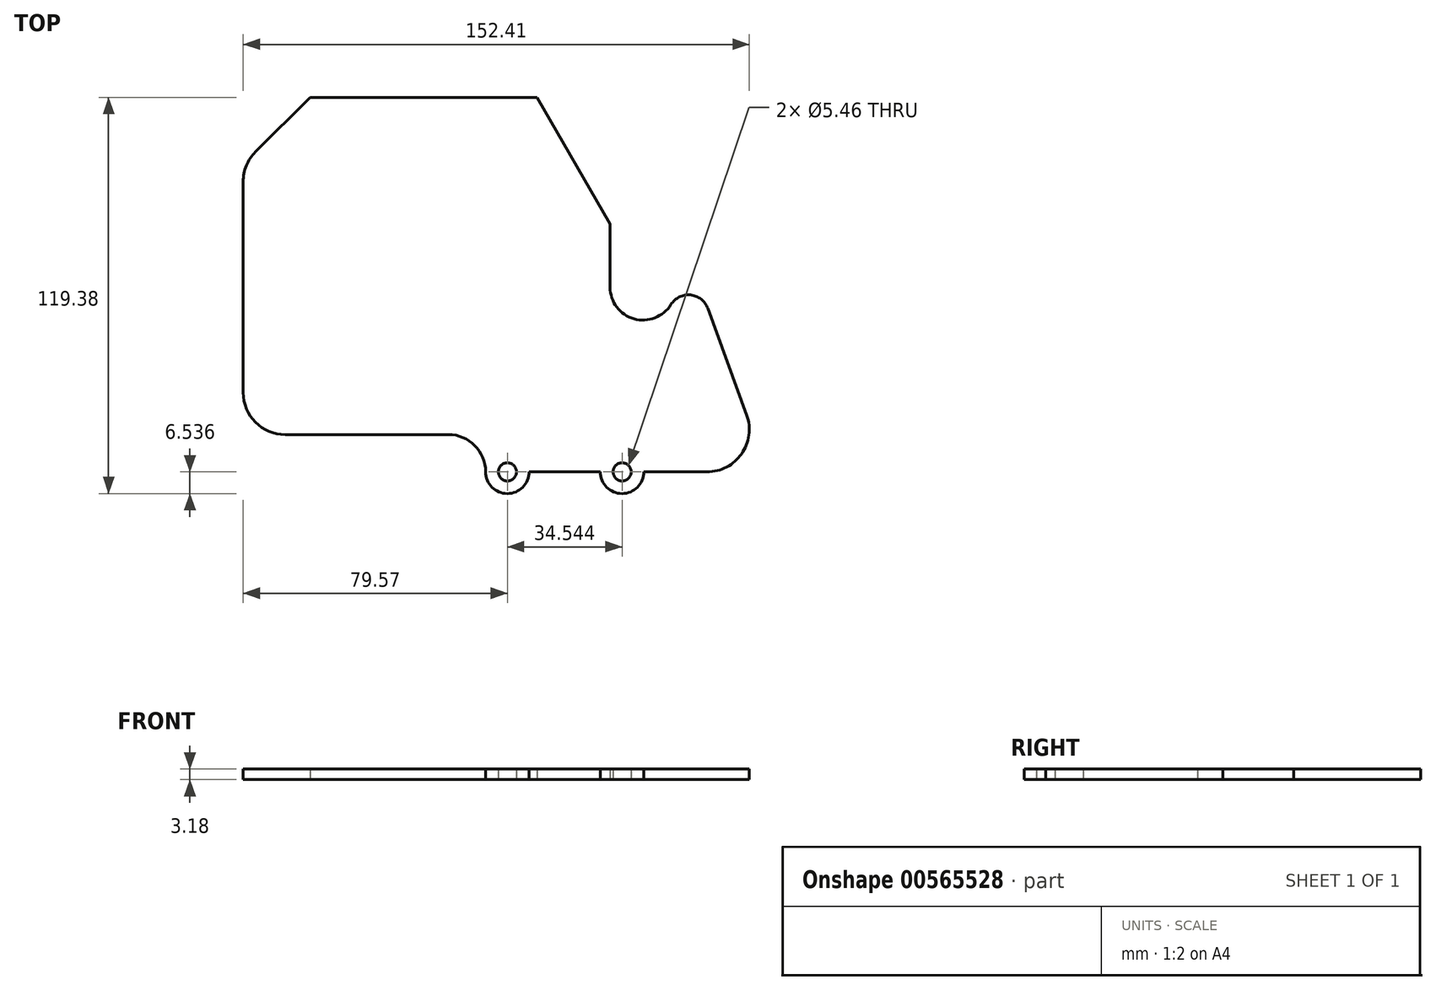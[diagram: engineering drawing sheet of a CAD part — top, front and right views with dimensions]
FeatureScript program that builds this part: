
annotation { "Feature Type Name" : "Feature", "Feature Type Description" : "" }
export const myFeature = defineFeature(function(context is Context, id is Id, definition is map)
    precondition{}
    {
        {
            var Q0;
            Q0=qCreatedBy(makeId("Top.planeOp"),FACE);
            var sketch = newSketch(context, id + "F0", { "sketchPlane" : qUnion([Q0])});
            skLineSegment(sketch, "E0", {"start": v(-55.24, 31.82) * mm, "end": v(-55.24, -31.68) * mm});
            skLineSegment(sketch, "E1", {"start": v(-42.54, -44.38) * mm, "end": v(6.54, -44.38) * mm});
            skLineSegment(sketch, "E2", {"start": v(-51.53, 40.8) * mm, "end": v(-35.1, 57.22) * mm});
            skPoint(sketch, "E3.visualSharp", {"position": v(-55.24, -44.38) * mm});
            skArc(sketch, "E3.filletArc", {"start": v(-55.24, -31.68) * mm, "mid": v(-51.53, -40.66) * mm, "end": v(-42.54, -44.38) * mm});
            skPoint(sketch, "E4.visualSharp", {"position": v(-55.24, 37.08) * mm});
            skArc(sketch, "E4.filletArc", {"start": v(-51.53, 40.8) * mm, "mid": v(-54.28, 36.68) * mm, "end": v(-55.24, 31.82) * mm});
            skLineSegment(sketch, "E5", {"start": v(84.66, -6.36) * mm, "end": v(96.39, -38.58) * mm});
            skArc(sketch, "E6", {"start": v(84.46, -55.62) * mm, "mid": v(94.86, -50.2) * mm, "end": v(96.39, -38.58) * mm});
            skLineSegment(sketch, "E7", {"start": v(84.46, -55.62) * mm, "end": v(65.4, -55.62) * mm});
            skCircle(sketch, "E8", {"center": v(24.32, -55.62) * mm, "radius": 2.73 * mm});
            skCircle(sketch, "E9", {"center": v(58.86, -55.62) * mm, "radius": 2.73 * mm});
            skArc(sketch, "E10.filletArc", {"start": v(17.78, -55.62) * mm, "mid": v(14.49, -47.68) * mm, "end": v(6.54, -44.38) * mm});
            skLineSegment(sketch, "E11", {"start": v(-43.39, -62.16) * mm, "end": v(97.16, -62.16) * mm, "construction": true});
            skLineSegment(sketch, "E12", {"start": v(97.16, -10.36) * mm, "end": v(97.16, -111.58) * mm, "construction": true});
            skArc(sketch, "E13", {"start": v(84.66, -6.36) * mm, "mid": v(79.47, -2.32) * mm, "end": v(73.57, -5.22) * mm});
            skArc(sketch, "E14", {"start": v(55.24, 0) * mm, "mid": v(62.44, -9.53) * mm, "end": v(73.57, -5.22) * mm});
            skLineSegment(sketch, "E15", {"start": v(65.15, -2.28) * mm, "end": v(148.92, -2.28) * mm, "construction": true});
            skArc(sketch, "E16", {"start": v(17.78, -55.62) * mm, "mid": v(24.32, -62.16) * mm, "end": v(30.86, -55.62) * mm});
            skArc(sketch, "E17", {"start": v(52.32, -55.62) * mm, "mid": v(58.86, -62.16) * mm, "end": v(65.4, -55.62) * mm});
            skLineSegment(sketch, "E18", {"start": v(30.86, -55.62) * mm, "end": v(52.32, -55.62) * mm});
            skLineSegment(sketch, "E19", {"start": v(55.24, 0) * mm, "end": v(55.24, 19.05) * mm});
            skLineSegment(sketch, "E20", {"start": v(55.25, 19.05) * mm, "end": v(33.2, 57.22) * mm});
            skLineSegment(sketch, "E21", {"start": v(48.99, -9.9) * mm, "end": v(136.6, -9.9) * mm, "construction": true});
            skLineSegment(sketch, "E22", {"start": v(-35.1, 57.22) * mm, "end": v(33.2, 57.22) * mm});
            skSolve(sketch);
        }
        {
            var Q0;
            Q0=makeQuery(id+"F0.imprint","IMPRINT",FACE,{"disambiguationData":[TD([[makeQuery(id+"F0.imprint","IMPRINT",EDGE,{"derivedFrom":sQuery(id+"F0.wireOp",EDGE,"E0")}),1.0]])]});
            extrude(context, id + "F1", {"entities" : qUnion([Q0]), "depth" : 3.17 * mm, "offsetDistance" : 25.4 * mm});
        }
    });
